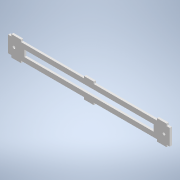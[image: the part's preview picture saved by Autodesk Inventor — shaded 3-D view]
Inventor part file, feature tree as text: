
AUTODESK INVENTOR PART (.ipt)
format: ipt  version: 2022 (Build 260153000, 153)  size: 144,384 bytes
history: native  units: mm
features: other x3, extrude x1, reference x1
ambient origin geometry x8: Origin, YZ Plane, XZ Plane, XY Plane, X Axis, Y Axis, Z Axis, Center Point
bodies: Body1 (feature_tree)
feature tree (5):
  extrude  "Extrusion4"  Depth=250.0mm
  reference  "Reference2"
  other  "<userpath>\OneDrive\Escritorio\Mini_Proyecto_Diseno\Diseno_18012\Modelo_MPD\Carril.iam"
  other  "Carril.iam"
  other  "Tope_Carril:1"
